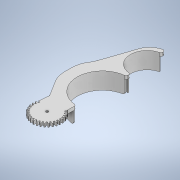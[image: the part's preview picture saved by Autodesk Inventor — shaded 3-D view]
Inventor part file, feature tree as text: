
AUTODESK INVENTOR PART (.ipt)
format: ipt  version: 2021 (Build 250183000, 183)  size: 580,096 bytes
history: native  units: mm
features: sketch x13, extrude x12, fillet x6
ambient origin geometry x8: Origin, YZ Plane, XZ Plane, XY Plane, X Axis, Y Axis, Z Axis, Center Point
bodies: Solid1 (feature_tree)
feature tree (31):
  extrude  "Extrusion1"  Depth=30.0mm
  extrude  "Extrusion4"  Depth=0.5mm
  extrude  "Extrusion6"  Depth=310.0mm TaperAngle=360.0deg
  extrude  "Extrusion9"  Depth=30.0mm
  extrude  "Extrusion10"  Depth=4.0mm TaperAngle=0.0deg
  extrude  "Extrusion11"  Depth=2.0mm
  fillet  "Fillet4"  Radius=2.0mm
  sketch  "Sketch14"  dims[d49=40.0mm d50=20.0mm d51=0.0mm]
  extrude  "Extrusion12"  Depth=10.0mm TaperAngle=0.0deg
  fillet  "Fillet5"  Radius=3.0mm
  fillet  "Fillet6"  Radius=10.0mm
  fillet  "Fillet7"  Radius=40.0mm
  fillet  "Fillet8"  Radius=10.0mm
  extrude  "Extrusion13"  Depth=20.0mm
  fillet  "Fillet9"  Radius=5.0mm
  extrude  "Extrusion14"  Depth=4.0mm TaperAngle=0.0deg
  extrude  "Extrusion5"  Depth=20.0mm TaperAngle=0.0deg
  extrude  "Extrusion2"  Depth=4.0mm TaperAngle=0.0deg
  extrude  "Extrusion3"  Depth=30.0mm
  sketch  "Sketch1"  dims[d0=30.0mm d1=35.0mm]
  sketch  "Sketch2"  dims[d2=0.5mm d4=0.5mm]
  sketch  "Sketch3"  dims[d6=0.1mm d7=310.0mm d9=360.0deg]
  sketch  "Sketch4"  dims[d13=60.0mm d14=30.0mm]
  sketch  "Sketch5"  dims[d15=10.0mm d19=4.0mm d20=0.0mm]
  sketch  "Sketch6"  dims[d22=10.0mm d23=0.1mm d24=2.0mm]
  sketch  "Sketch10"  dims[d25=3.0mm d26=0.0mm d27=3.0mm d28=0.0mm d29=3.0mm d30=10.0mm d31=0.0mm d32=40.0mm d33=10.0mm d34=0.0mm]
  sketch  "Sketch12"  dims[d35=20.0mm d36=0.0mm d43=22.0mm d44=5.0mm d45=0.0mm]
  sketch  "Sketch13"  dims[d46=40.0mm d47=4.0mm d48=0.0mm]
  sketch  "Sketch15"  dims[d52=21.0mm d53=4.0mm d54=0.0mm]
  sketch  "Sketch16"  dims[d55=1614.0mm d56=30.0mm]
  sketch  "Sketch17"  dims[d57=2.0mm d58=2.0mm d59=4.0mm d60=0.0mm d61=2.25mm d62=20.0mm d63=0.0mm d11=0.5mm d12=0.872665mm d64=0.5mm d65=0.872665mm d66=0.5mm d67=0.872665mm]
